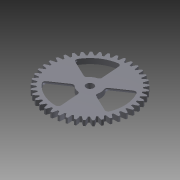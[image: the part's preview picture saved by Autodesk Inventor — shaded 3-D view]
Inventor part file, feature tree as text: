
AUTODESK INVENTOR PART (.ipt)
format: ipt  version: 2014 SP2 (Build 180246200, 246)  size: 537,088 bytes
history: native  units: mm (DEFAULTED — no unit token found)
features: sketch x4, plane x3, other x3, extrude x2, hole x1, chamfer x1, fillet x1, reference x1
ambient origin geometry x8: Origin, YZ Plane, XZ Plane, XY Plane, X Axis, Y Axis, Z Axis, Center Point
bodies: Solid1 (feature_tree)
feature tree (16):
  extrude  "Extrusion1"  Depth=6.0mm TaperAngle=0.0deg
  plane  "Work Plane2"
  plane  "Work Plane8"
  plane  "Work Plane9"
  other  "Spur Gear"
  hole  "Hole1"  [1 undecoded]
  extrude  "Extrusion2"  Depth=0.766242mm TaperAngle=0.0deg
  chamfer  "Chamfer1"  [1 undecoded]
  fillet  "Fillet1"  Radius=71.527931mm
  sketch  "Sketch1"  dims[d0=96.669411mm d1=6.0mm d2=0.0mm]
  sketch  "Sketch2"  dims[d3=93.099847mm d4=10.0mm d5=0.0mm]
  other  "Srf1"
  sketch  "Sketch3"  dims[d16=71.527931mm d17=0.0mm d34=0.766242mm]
  sketch  "Sketch4"  dims[d39=0.0mm d41=0.0mm d43=71.527931mm d46=71.527931mm d47=0.0mm d48=0.0mm d49=8.5mm d50=6.0mm d51=4.0mm d52=2.0mm d53=90.0deg d54=8.0mm d55=20.594885mm d56=4.0mm d57=10.0mm d58=0.0mm d59=5.0mm d60=2.0mm d61=45.0deg d62=3.0mm]
  reference  "Reference1"
  other  "Pitch Diameter"
note: 2 required parameter values undecoded (feature->parameter linkage not recoverable at this tier; creation-order binding heuristic only, values carry confidence <= 0.55)
